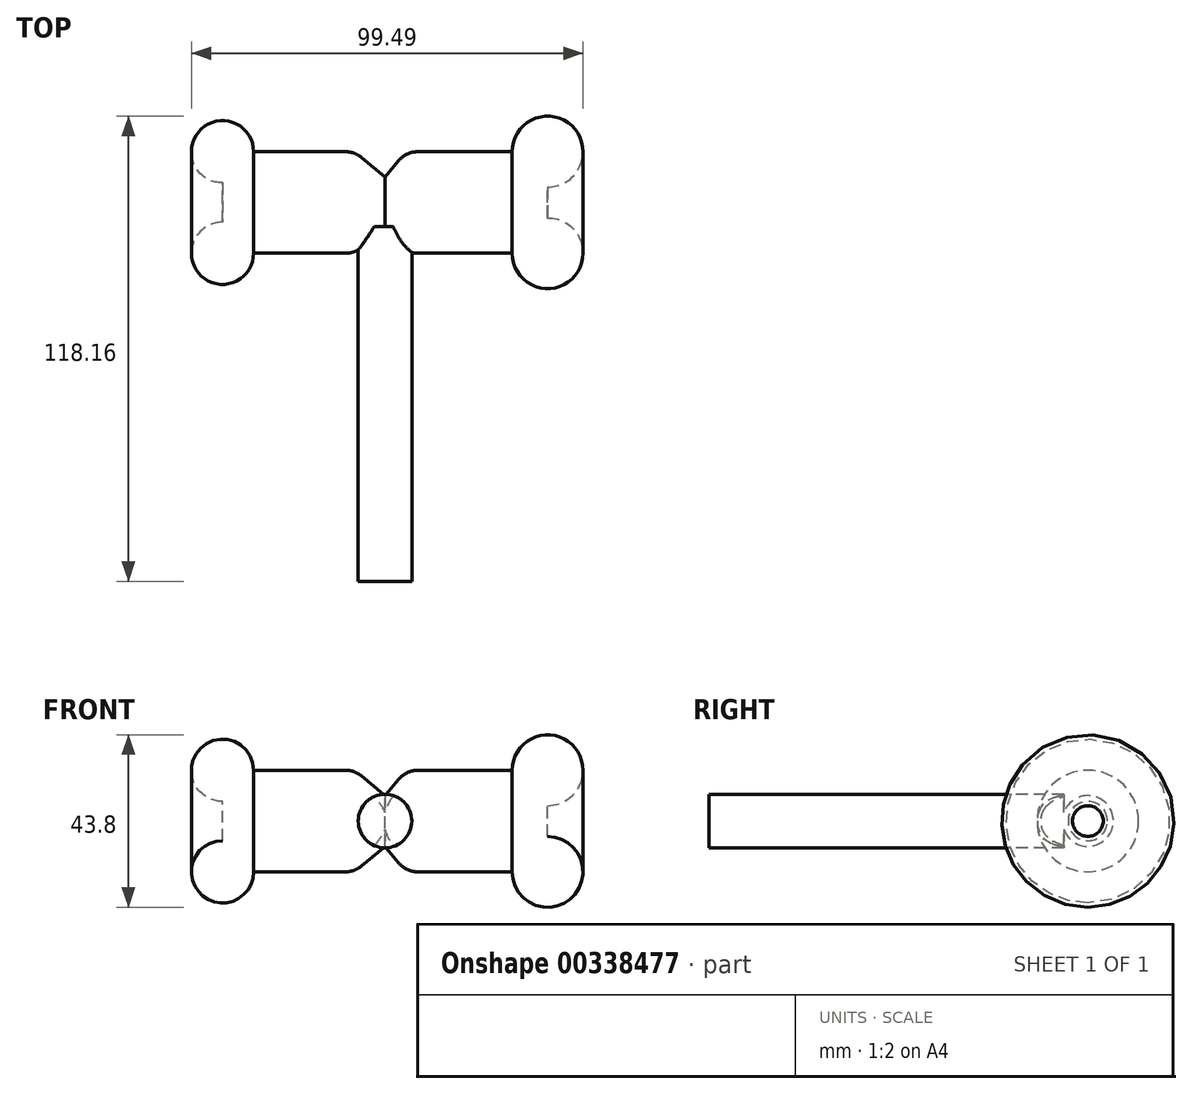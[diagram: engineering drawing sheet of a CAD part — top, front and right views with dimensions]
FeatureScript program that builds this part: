
annotation { "Feature Type Name" : "Feature", "Feature Type Description" : "" }
export const myFeature = defineFeature(function(context is Context, id is Id, definition is map)
    precondition{}
    {
        {
            var Q0;
            Q0=qCreatedBy(makeId("Top.planeOp"),FACE);
            var sketch = newSketch(context, id + "F0", { "sketchPlane" : qUnion([Q0])});
            skLineSegment(sketch, "E0.bottom", {"start": v(41.3, 39.36) * mm, "end": v(-41.3, 39.36) * mm});
            skLineSegment(sketch, "E0.top", {"start": v(32.3, 52.26) * mm, "end": v(8.35, 52.26) * mm});
            skLineSegment(sketch, "E0.left", {"start": v(41.3, 39.36) * mm, "end": v(41.3, 43.27) * mm});
            skLineSegment(sketch, "E0.right", {"start": v(-41.3, 39.36) * mm, "end": v(-41.3, 44.36) * mm});
            skPoint(sketch, "E0.middle", {"position": v(0, 45.81) * mm});
            skLineSegment(sketch, "E1", {"start": v(-5.98, 50.8) * mm, "end": v(0, 45.81) * mm});
            skLineSegment(sketch, "E2", {"start": v(0, 45.81) * mm, "end": v(3.47, 49.98) * mm});
            skArc(sketch, "E3", {"start": v(41.3, 43.27) * mm, "mid": v(47.66, 58.63) * mm, "end": v(32.3, 52.26) * mm});
            skArc(sketch, "E4", {"start": v(-33.39, 52.26) * mm, "mid": v(-46.89, 57.86) * mm, "end": v(-41.3, 44.36) * mm});
            skLineSegment(sketch, "E5.trimOffspring", {"start": v(-10.04, 52.26) * mm, "end": v(-33.39, 52.26) * mm});
            skPoint(sketch, "E6.visualSharp", {"position": v(-7.74, 52.26) * mm});
            skArc(sketch, "E6.filletArc", {"start": v(-5.98, 50.8) * mm, "mid": v(-7.88, 51.89) * mm, "end": v(-10.04, 52.26) * mm});
            skPoint(sketch, "E7.visualSharp", {"position": v(5.38, 52.26) * mm});
            skArc(sketch, "E7.filletArc", {"start": v(8.35, 52.26) * mm, "mid": v(5.66, 51.67) * mm, "end": v(3.47, 49.98) * mm});
            skSolve(sketch);
        }
        {
            var Q0;
            Q0 = qSketchRegion(id + "F0", true);
            var Q1;
            Q1=sQuery(id+"F0.wireOp",EDGE,"E0.bottom");
            revolve(context, id + "F1", {"entities" : qUnion([Q0]), "axis" : qUnion([Q1]), "revolveType" : RevolveType.FULL});
        }
        {
            var Q0;
            Q0=qCreatedBy(makeId("Front.planeOp"),FACE);
            var sketch = newSketch(context, id + "F2", { "sketchPlane" : qUnion([Q0])});
            skCircle(sketch, "E8", {"center": v(0, 0) * mm, "radius": 6.8 * mm});
            skSolve(sketch);
        }
        {
            var Q0;
            Q0 = qSketchRegion(id + "F2", true);
            extrude(context, id + "F3", {"entities" : qUnion([Q0]), "operationType" : NewBodyOperationType.ADD, "oppositeDirection" : true, "depth" : 33.27 * mm});
        }
        {
            var Q0;
            Q0 = qSketchRegion(id + "F2", true);
            extrude(context, id + "F4", {"entities" : qUnion([Q0]), "operationType" : NewBodyOperationType.ADD, "depth" : 56.9 * mm});
        }
    });
